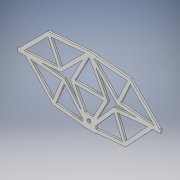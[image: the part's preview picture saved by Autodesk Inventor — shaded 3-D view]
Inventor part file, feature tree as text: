
AUTODESK INVENTOR PART (.ipt)
format: ipt  version: 2018 (Build 220112000, 112)  size: 238,080 bytes
history: native  units: in
note: dims shown in document units (in); Inventor stores cm internally (conversion verified against a paired STEP export)
features: extrude x1, sketch x1
ambient origin geometry x8: Origin, YZ Plane, XZ Plane, XY Plane, X Axis, Y Axis, Z Axis, Center Point
bodies: Solid1 (feature_tree)
feature tree (2):
  extrude  "Extrusion1"  Depth=0.125in
  sketch  "Sketch1"  dims[d1=10.5in d2=5.0in d4=45.0deg d6=0.0327in d7=1.2041in d9=0.0327in d10=2.5in d11=5.25in d12=0.125in d13=135.0deg d14=0.125in d16=135.0deg d17=0.125in d18=2.5in d19=1.2041in d20=45.0deg d21=45.0deg d22=1.25in d23=1.25in d24=2.375in d25=5.25in d26=0.125in d27=0.9045in d29=1.2012in d30=2.625in d31=1.875in d32=0.5in d33=4.75in d34=1.0in d37=0.5583in d38=0.2791in d45=0.25in d46=0.125in d47=0.125in d48=0.125in d49=0.125in d50=0.125in d51=0.125in d53=0.25in d54=0.25in d55=0.25in d56=0.25in d57=0.125in d58=0.25in d59=0.25in d60=0.125in d61=0.125in d62=0.25in d63=0.125in d67=0.25in d68=0.125in d69=0.25in d70=0.25in d71=0.25in d72=0.125in d73=0.125in d74=0.25in d75=0.25in d76=0.125in d77=1.043in d78=0.25in d80=0.125in d81=0.0in]
